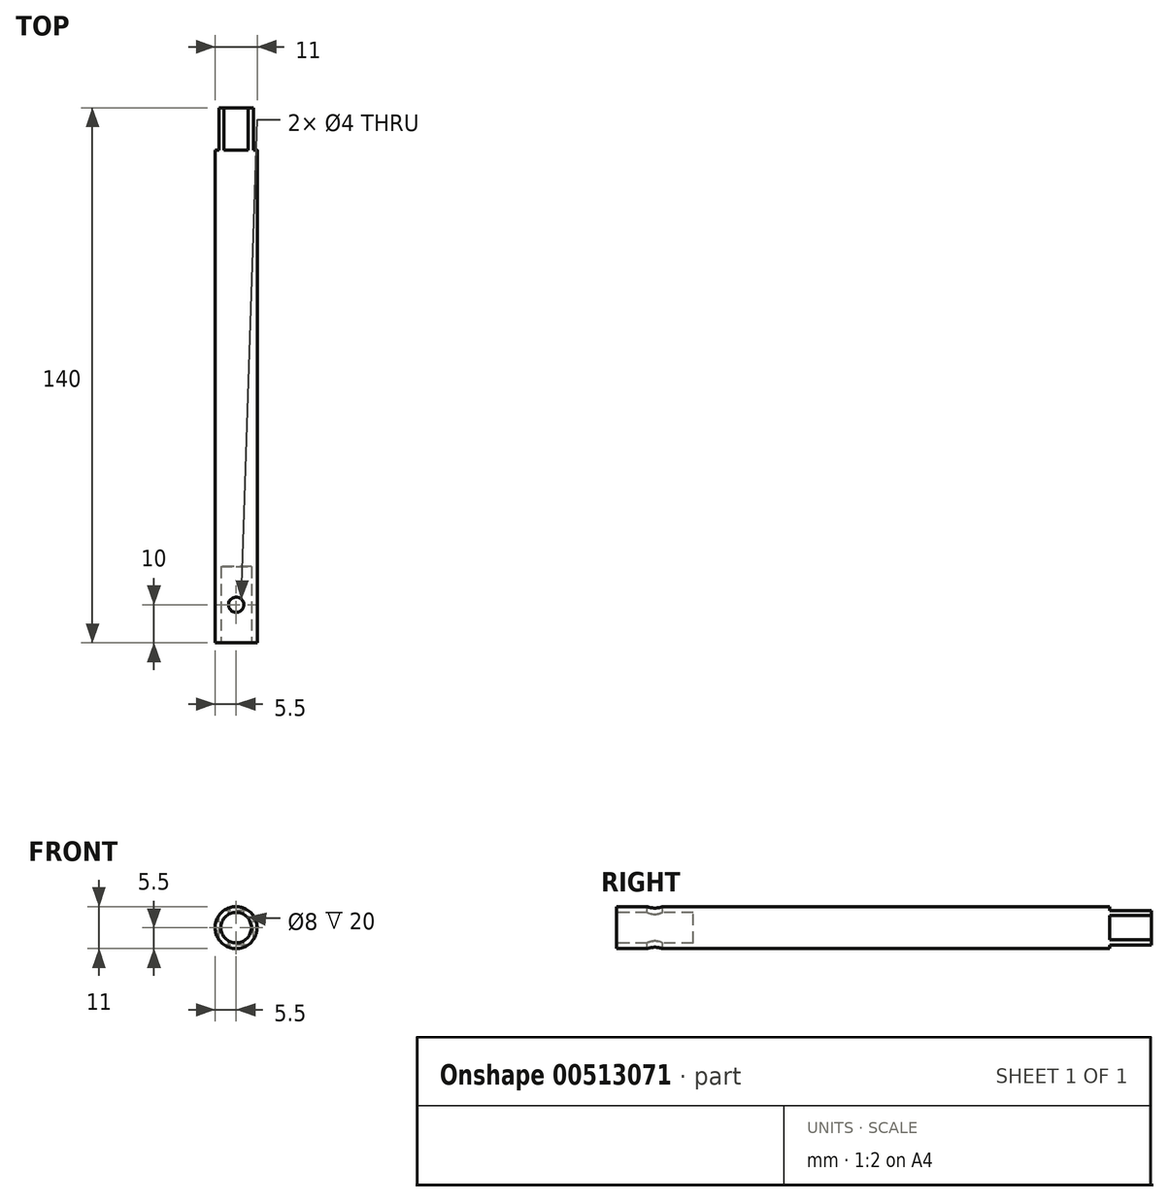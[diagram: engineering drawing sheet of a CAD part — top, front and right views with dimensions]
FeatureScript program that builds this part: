
annotation { "Feature Type Name" : "Feature", "Feature Type Description" : "" }
export const myFeature = defineFeature(function(context is Context, id is Id, definition is map)
    precondition{}
    {
        {
            var Q0;
            Q0=qCreatedBy(makeId("Front.planeOp"),FACE);
            var sketch = newSketch(context, id + "F0", { "sketchPlane" : qUnion([Q0])});
            skCircle(sketch, "E0", {"center": v(0, 0) * mm, "radius": 5.5 * mm});
            skSolve(sketch);
        }
        {
            var Q0;
            Q0=qSketchRegion(id+"F0",true);
            extrude(context, id + "F1", {"entities" : qUnion([Q0]), "depth" : 140 * mm});
        }
        {
            var Q0;
            Q0=makeQuery(id+"F1.opExtrude","CAP_FACE",FACE,{"disambiguationData":[OSD([sQuery(id+"F0.wireOp",EDGE,"E0")])],"isStart":false});
            var sketch = newSketch(context, id + "F2", { "sketchPlane" : qUnion([Q0])});
            skCircle(sketch, "E1", {"center": v(0, 0) * mm, "radius": 4 * mm});
            skSolve(sketch);
        }
        {
            var Q0;
            Q0=qSketchRegion(id+"F2",true);
            extrude(context, id + "F3", {"entities" : qUnion([Q0]), "operationType" : NewBodyOperationType.REMOVE, "oppositeDirection" : true, "depth" : 20 * mm});
        }
        {
            var Q0;
            Q0=makeQuery(id+"F1.opExtrude","CAP_FACE",FACE,{"disambiguationData":[OSD([sQuery(id+"F0.wireOp",EDGE,"E0")])],"isStart":true});
            var sketch = newSketch(context, id + "F4", { "sketchPlane" : qUnion([Q0])});
            skLineSegment(sketch, "E2.bottom", {"start": v(-4.5, -4.5) * mm, "end": v(4.5, -4.5) * mm});
            skLineSegment(sketch, "E2.top", {"start": v(-4.5, 4.5) * mm, "end": v(4.5, 4.5) * mm});
            skLineSegment(sketch, "E2.left", {"start": v(-4.5, -4.5) * mm, "end": v(-4.5, 4.5) * mm});
            skLineSegment(sketch, "E2.right", {"start": v(4.5, -4.5) * mm, "end": v(4.5, 4.5) * mm});
            skPoint(sketch, "E2.middle", {"position": v(0, 0) * mm});
            skSolve(sketch);
        }
        {
            var Q0;
            {var subQ0=sQuery(id+"F4.wireOp",EDGE,"E2.right");var subQ1=makeQuery(id+"F1.opExtrude","CAP_EDGE",EDGE,{"disambiguationData":[OSD([sQuery(id+"F0.wireOp",EDGE,"E0")])],"isStart":true});var subQ2=makeQuery(id+"F4.imprint","INTERSECT",VERTEX,{"disambiguationData":[OD(0.0)],"derivedFrom":[subQ1,subQ0]});Q0=makeQuery(id+"F4.imprint","IMPRINT",FACE,{"disambiguationData":[TD([[makeQuery(id+"F4.imprint","IMPRINT",EDGE,{"disambiguationData":[TD([[subQ2,-1.0]])],"derivedFrom":subQ0}),-1.0]])]});}
            var Q1;
            {var subQ0=sQuery(id+"F4.wireOp",EDGE,"E2.top");var subQ1=makeQuery(id+"F1.opExtrude","CAP_EDGE",EDGE,{"disambiguationData":[OSD([sQuery(id+"F0.wireOp",EDGE,"E0")])],"isStart":true});var subQ2=makeQuery(id+"F4.imprint","INTERSECT",VERTEX,{"disambiguationData":[OD(0.0)],"derivedFrom":[subQ1,subQ0]});Q1=makeQuery(id+"F4.imprint","IMPRINT",FACE,{"disambiguationData":[TD([[makeQuery(id+"F4.imprint","IMPRINT",EDGE,{"disambiguationData":[TD([[subQ2,-1.0]])],"derivedFrom":subQ0}),1.0]])]});}
            var Q2;
            {var subQ0=sQuery(id+"F4.wireOp",EDGE,"E2.left");var subQ1=makeQuery(id+"F1.opExtrude","CAP_EDGE",EDGE,{"disambiguationData":[OSD([sQuery(id+"F0.wireOp",EDGE,"E0")])],"isStart":true});var subQ2=makeQuery(id+"F4.imprint","INTERSECT",VERTEX,{"disambiguationData":[OD(0.0)],"derivedFrom":[subQ1,subQ0]});Q2=makeQuery(id+"F4.imprint","IMPRINT",FACE,{"disambiguationData":[TD([[makeQuery(id+"F4.imprint","IMPRINT",EDGE,{"disambiguationData":[TD([[subQ2,-1.0]])],"derivedFrom":subQ0}),1.0]])]});}
            var Q3;
            {var subQ0=sQuery(id+"F4.wireOp",EDGE,"E2.bottom");var subQ1=makeQuery(id+"F1.opExtrude","CAP_EDGE",EDGE,{"disambiguationData":[OSD([sQuery(id+"F0.wireOp",EDGE,"E0")])],"isStart":true});var subQ2=makeQuery(id+"F4.imprint","INTERSECT",VERTEX,{"disambiguationData":[OD(0.0)],"derivedFrom":[subQ1,subQ0]});Q3=makeQuery(id+"F4.imprint","IMPRINT",FACE,{"disambiguationData":[TD([[makeQuery(id+"F4.imprint","IMPRINT",EDGE,{"disambiguationData":[TD([[subQ2,-1.0]])],"derivedFrom":subQ0}),-1.0]])]});}
            extrude(context, id + "F5", {"entities" : qUnion([Q0, Q1, Q2, Q3]), "operationType" : NewBodyOperationType.REMOVE, "oppositeDirection" : true, "depth" : 11 * mm});
        }
        {
            var Q0;
            Q0=qCreatedBy(makeId("Top.planeOp"),FACE);
            var sketch = newSketch(context, id + "F6", { "sketchPlane" : qUnion([Q0])});
            skCircle(sketch, "E3", {"center": v(0, -130) * mm, "radius": 2 * mm});
            skSolve(sketch);
        }
        {
            var Q0;
            Q0 = qSketchRegion(id + "F6", true);
            extrude(context, id + "F7", {"entities" : qUnion([Q0]), "operationType" : NewBodyOperationType.REMOVE, "endBound" : BoundingType.SYMMETRIC, "oppositeDirection" : true, "depth" : 25 * mm});
        }
    });
